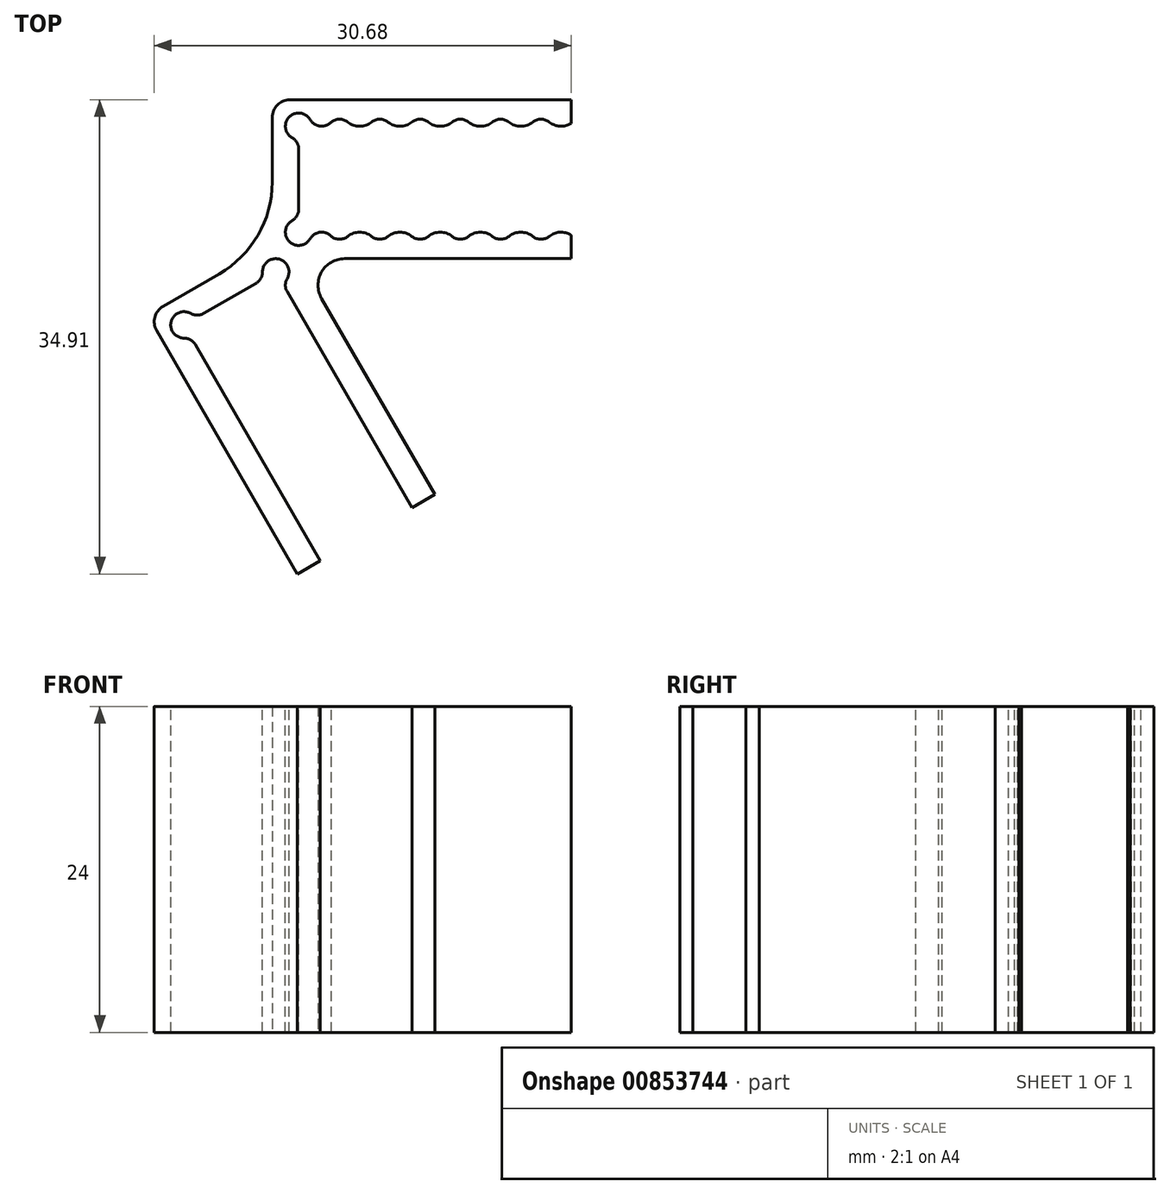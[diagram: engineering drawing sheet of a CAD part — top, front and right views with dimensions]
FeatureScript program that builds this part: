
annotation { "Feature Type Name" : "Feature", "Feature Type Description" : "" }
export const myFeature = defineFeature(function(context is Context, id is Id, definition is map)
    precondition{}
    {
        {
            var Q0;
            Q0=qCreatedBy(makeId("Top.planeOp"),FACE);
            var sketch = newSketch(context, id + "F0", { "sketchPlane" : qUnion([Q0])});
            skCircle(sketch, "E0.cCircle", {"center": v(0, 0) * mm, "radius": 33.77 * mm, "construction": true});
            skLineSegment(sketch, "E0.0", {"start": v(58.5, 33.77) * mm, "end": v(0, -67.55) * mm, "construction": true});
            skLineSegment(sketch, "E0.1", {"start": v(0, -67.55) * mm, "end": v(-58.5, 33.77) * mm, "construction": true});
            skLineSegment(sketch, "E0.2", {"start": v(-58.5, 33.77) * mm, "end": v(58.5, 33.77) * mm, "construction": true});
            skPoint(sketch, "E0.0.midPoint", {"position": v(29.25, -16.89) * mm});
            skSolve(sketch);
        }
        {
            var Q0;
            Q0=qCreatedBy(makeId("Top.planeOp"),FACE);
            var sketch = newSketch(context, id + "F1", { "sketchPlane" : qUnion([Q0])});
            skLineSegment(sketch, "E1", {"start": v(-58.5, 33.77) * mm, "end": v(0, 0) * mm, "construction": true});
            skLineSegment(sketch, "E2.0", {"start": v(-58.5, 35.72) * mm, "end": v(-38.45, 35.72) * mm});
            skLineSegment(sketch, "E3", {"start": v(-58.5, 35.72) * mm, "end": v(-58.5, 43.52) * mm});
            skLineSegment(sketch, "E4", {"start": v(-58.5, 43.52) * mm, "end": v(-38.45, 43.52) * mm});
            skLineSegment(sketch, "E5.0", {"start": v(-60.45, 45.47) * mm, "end": v(-38.45, 45.47) * mm});
            skLineSegment(sketch, "E5.1", {"start": v(-60.45, 34.9) * mm, "end": v(-60.45, 45.47) * mm});
            skLineSegment(sketch, "E5.2", {"start": v(-58.5, 33.77) * mm, "end": v(-38.45, 33.77) * mm});
            skLineSegment(sketch, "E6", {"start": v(-38.45, 45.47) * mm, "end": v(-38.45, 43.52) * mm});
            skLineSegment(sketch, "E7.trimOffspring", {"start": v(-38.45, 35.72) * mm, "end": v(-38.45, 33.77) * mm});
            skLineSegment(sketch, "E8.MirrorCS", {"start": v(-50.16, 15.44) * mm, "end": v(-48.48, 16.41) * mm});
            skLineSegment(sketch, "E9.MirrorCS", {"start": v(-69.6, 29.61) * mm, "end": v(-58.6, 10.56) * mm});
            skLineSegment(sketch, "E10.MirrorCS", {"start": v(-66.94, 28.9) * mm, "end": v(-56.92, 11.54) * mm});
            skLineSegment(sketch, "E11.MirrorCS", {"start": v(-60.19, 32.8) * mm, "end": v(-66.94, 28.9) * mm});
            skLineSegment(sketch, "E12.MirrorCS", {"start": v(-60.45, 34.9) * mm, "end": v(-69.6, 29.61) * mm});
            skLineSegment(sketch, "E13.MirrorCS", {"start": v(-58.6, 10.56) * mm, "end": v(-56.92, 11.54) * mm});
            skLineSegment(sketch, "E14", {"start": v(-58.5, 33.77) * mm, "end": v(-48.48, 16.41) * mm});
            skLineSegment(sketch, "E15", {"start": v(-50.16, 15.44) * mm, "end": v(-60.19, 32.8) * mm});
            skSolve(sketch);
        }
        {
            var Q0;
            Q0 = qSketchRegion(id + "F1", true);
            extrude(context, id + "F2", {"entities" : qUnion([Q0]), "depth" : 24 * mm, "offsetDistance" : 25 * mm});
        }
        {
            var Q0;
            Q0=makeQuery(id+"F2.opExtrude","SWEPT_EDGE",EDGE,{"disambiguationData":[OSD([sQuery(id+"F1.wireOp",EDGE,"E5.2"),sQuery(id+"F1.wireOp",EDGE,"E14")])]});
            fillet(context, id + "F3", {"entities" : qUnion([Q0]), "radius" : (7.8 / 4) * mm, "tangentPropagation" : true, "allowEdgeOverflow" : false});
        }
        {
            var Q0;
            Q0=makeQuery(id+"F2.opExtrude","SWEPT_EDGE",EDGE,{"disambiguationData":[OSD([sQuery(id+"F1.wireOp",EDGE,"E5.0"),sQuery(id+"F1.wireOp",EDGE,"E5.1")])]});
            var Q1;
            Q1=makeQuery(id+"F2.opExtrude","SWEPT_EDGE",EDGE,{"disambiguationData":[OSD([sQuery(id+"F1.wireOp",EDGE,"E9.MirrorCS"),sQuery(id+"F1.wireOp",EDGE,"E12.MirrorCS")])]});
            fillet(context, id + "F4", {"entities" : qUnion([Q0, Q1]), "radius" : (7.8 / 6) * mm, "tangentPropagation" : true, "allowEdgeOverflow" : false});
        }
        {
            var Q0;
            Q0=makeQuery(id+"F2.opExtrude","SWEPT_EDGE",EDGE,{"disambiguationData":[OSD([sQuery(id+"F1.wireOp",EDGE,"E5.1"),sQuery(id+"F1.wireOp",EDGE,"E12.MirrorCS")])]});
            fillet(context, id + "F5", {"entities" : qUnion([Q0]), "radius" : 7.8 * mm, "tangentPropagation" : true, "allowEdgeOverflow" : false});
        }
        {
            var Q0;
            Q0=makeQuery(id+"F2.opExtrude","CAP_FACE",FACE,{"disambiguationData":[OSD([sQuery(id+"F1.wireOp",EDGE,"E2.0"),sQuery(id+"F1.wireOp",EDGE,"E3"),sQuery(id+"F1.wireOp",EDGE,"E4"),sQuery(id+"F1.wireOp",EDGE,"E5.0"),sQuery(id+"F1.wireOp",EDGE,"E5.1"),sQuery(id+"F1.wireOp",EDGE,"E5.2"),sQuery(id+"F1.wireOp",EDGE,"E6"),sQuery(id+"F1.wireOp",EDGE,"E7.trimOffspring"),sQuery(id+"F1.wireOp",EDGE,"E8.MirrorCS"),sQuery(id+"F1.wireOp",EDGE,"E9.MirrorCS"),sQuery(id+"F1.wireOp",EDGE,"E10.MirrorCS"),sQuery(id+"F1.wireOp",EDGE,"E11.MirrorCS"),sQuery(id+"F1.wireOp",EDGE,"E12.MirrorCS"),sQuery(id+"F1.wireOp",EDGE,"E13.MirrorCS"),sQuery(id+"F1.wireOp",EDGE,"E14"),sQuery(id+"F1.wireOp",EDGE,"E15")])],"isStart":false});
            var sketch = newSketch(context, id + "F6", { "sketchPlane" : qUnion([Q0])});
            skCircle(sketch, "E16", {"center": v(-58.5, 43.52) * mm, "radius": 0.97 * mm});
            skCircle(sketch, "E17", {"center": v(-58.5, 35.72) * mm, "radius": 0.97 * mm});
            skCircle(sketch, "E18", {"center": v(-60.19, 32.8) * mm, "radius": 0.97 * mm});
            skCircle(sketch, "E19", {"center": v(-66.94, 28.9) * mm, "radius": 0.97 * mm});
            skSolve(sketch);
        }
        {
            var Q0;
            Q0 = qSketchRegion(id + "F6", true);
            extrude(context, id + "F7", {"entities" : qUnion([Q0]), "operationType" : NewBodyOperationType.REMOVE, "endBound" : BoundingType.THROUGH_ALL, "oppositeDirection" : true, "depth" : 25 * mm, "offsetDistance" : 25 * mm});
        }
        {
            var Q0;
            Q0=makeQuery(id+"F7.boolean.opBoolean","INTERSECT",EDGE,{"derivedFrom":[makeQuery(id+"F2.opExtrude","SWEPT_FACE",FACE,{"disambiguationData":[OSD([sQuery(id+"F1.wireOp",EDGE,"E4")])]}),makeQuery(id+"F7.opExtrude","SWEPT_FACE",FACE,{"disambiguationData":[OSD([sQuery(id+"F6.wireOp",EDGE,"E16")])]})]});
            var Q1;
            Q1=makeQuery(id+"F7.boolean.opBoolean","INTERSECT",EDGE,{"derivedFrom":[makeQuery(id+"F2.opExtrude","SWEPT_FACE",FACE,{"disambiguationData":[OSD([sQuery(id+"F1.wireOp",EDGE,"E3")])]}),makeQuery(id+"F7.opExtrude","SWEPT_FACE",FACE,{"disambiguationData":[OSD([sQuery(id+"F6.wireOp",EDGE,"E16")])]})]});
            var Q2;
            Q2=makeQuery(id+"F7.boolean.opBoolean","INTERSECT",EDGE,{"derivedFrom":[makeQuery(id+"F2.opExtrude","SWEPT_FACE",FACE,{"disambiguationData":[OSD([sQuery(id+"F1.wireOp",EDGE,"E3")])]}),makeQuery(id+"F7.opExtrude","SWEPT_FACE",FACE,{"disambiguationData":[OSD([sQuery(id+"F6.wireOp",EDGE,"E17")])]})]});
            var Q3;
            Q3=makeQuery(id+"F7.boolean.opBoolean","INTERSECT",EDGE,{"derivedFrom":[makeQuery(id+"F2.opExtrude","SWEPT_FACE",FACE,{"disambiguationData":[OSD([sQuery(id+"F1.wireOp",EDGE,"E11.MirrorCS")])]}),makeQuery(id+"F7.opExtrude","SWEPT_FACE",FACE,{"disambiguationData":[OSD([sQuery(id+"F6.wireOp",EDGE,"E18")])]})]});
            var Q4;
            Q4=makeQuery(id+"F7.boolean.opBoolean","INTERSECT",EDGE,{"derivedFrom":[makeQuery(id+"F2.opExtrude","SWEPT_FACE",FACE,{"disambiguationData":[OSD([sQuery(id+"F1.wireOp",EDGE,"E11.MirrorCS")])]}),makeQuery(id+"F7.opExtrude","SWEPT_FACE",FACE,{"disambiguationData":[OSD([sQuery(id+"F6.wireOp",EDGE,"E19")])]})]});
            var Q5;
            Q5=makeQuery(id+"F7.boolean.opBoolean","INTERSECT",EDGE,{"derivedFrom":[makeQuery(id+"F2.opExtrude","SWEPT_FACE",FACE,{"disambiguationData":[OSD([sQuery(id+"F1.wireOp",EDGE,"E10.MirrorCS")])]}),makeQuery(id+"F7.opExtrude","SWEPT_FACE",FACE,{"disambiguationData":[OSD([sQuery(id+"F6.wireOp",EDGE,"E19")])]})]});
            var Q6;
            Q6=makeQuery(id+"F7.boolean.opBoolean","INTERSECT",EDGE,{"derivedFrom":[makeQuery(id+"F2.opExtrude","SWEPT_FACE",FACE,{"disambiguationData":[OSD([sQuery(id+"F1.wireOp",EDGE,"E15")])]}),makeQuery(id+"F7.opExtrude","SWEPT_FACE",FACE,{"disambiguationData":[OSD([sQuery(id+"F6.wireOp",EDGE,"E18")])]})]});
            var Q7;
            Q7=makeQuery(id+"F7.boolean.opBoolean","INTERSECT",EDGE,{"derivedFrom":[makeQuery(id+"F2.opExtrude","SWEPT_FACE",FACE,{"disambiguationData":[OSD([sQuery(id+"F1.wireOp",EDGE,"E2.0")])]}),makeQuery(id+"F7.opExtrude","SWEPT_FACE",FACE,{"disambiguationData":[OSD([sQuery(id+"F6.wireOp",EDGE,"E17")])]})]});
            fillet(context, id + "F8", {"entities" : qUnion([Q0, Q1, Q2, Q3, Q4, Q5, Q6, Q7]), "radius" : (7.8 / 8) * mm, "tangentPropagation" : true, "allowEdgeOverflow" : false});
        }
        {
            var Q0;
            Q0=makeQuery(id+"F2.opExtrude","CAP_FACE",FACE,{"disambiguationData":[OSD([sQuery(id+"F1.wireOp",EDGE,"E2.0"),sQuery(id+"F1.wireOp",EDGE,"E3"),sQuery(id+"F1.wireOp",EDGE,"E4"),sQuery(id+"F1.wireOp",EDGE,"E5.0"),sQuery(id+"F1.wireOp",EDGE,"E5.1"),sQuery(id+"F1.wireOp",EDGE,"E5.2"),sQuery(id+"F1.wireOp",EDGE,"E6"),sQuery(id+"F1.wireOp",EDGE,"E7.trimOffspring"),sQuery(id+"F1.wireOp",EDGE,"E8.MirrorCS"),sQuery(id+"F1.wireOp",EDGE,"E9.MirrorCS"),sQuery(id+"F1.wireOp",EDGE,"E10.MirrorCS"),sQuery(id+"F1.wireOp",EDGE,"E11.MirrorCS"),sQuery(id+"F1.wireOp",EDGE,"E12.MirrorCS"),sQuery(id+"F1.wireOp",EDGE,"E13.MirrorCS"),sQuery(id+"F1.wireOp",EDGE,"E14"),sQuery(id+"F1.wireOp",EDGE,"E15")])],"isStart":false});
            var sketch = newSketch(context, id + "F9", { "sketchPlane" : qUnion([Q0])});
            skArc(sketch, "E20", {"start": v(-56.1, 35.42) * mm, "mid": v(-56.42, 35.65) * mm, "end": v(-56.81, 35.72) * mm});
            skArc(sketch, "E21", {"start": v(-56.1, 35.42) * mm, "mid": v(-55.5, 35.2) * mm, "end": v(-54.88, 35.42) * mm});
            skLineSegment(sketch, "E22", {"start": v(-56.77, 35.42) * mm, "end": v(-38.45, 35.42) * mm, "construction": true});
            skArc(sketch, "E23", {"start": v(-54.88, 35.42) * mm, "mid": v(-54.01, 35.72) * mm, "end": v(-53.14, 35.42) * mm});
            skArc(sketch, "E24.1.0.0", {"start": v(-53.14, 35.42) * mm, "mid": v(-52.53, 35.2) * mm, "end": v(-51.92, 35.42) * mm});
            skArc(sketch, "E24.1.0.1", {"start": v(-51.92, 35.42) * mm, "mid": v(-51.04, 35.72) * mm, "end": v(-50.17, 35.42) * mm});
            skArc(sketch, "E24.2.0.0", {"start": v(-50.17, 35.42) * mm, "mid": v(-49.56, 35.2) * mm, "end": v(-48.95, 35.42) * mm});
            skArc(sketch, "E24.2.0.1", {"start": v(-48.95, 35.42) * mm, "mid": v(-48.08, 35.72) * mm, "end": v(-47.2, 35.42) * mm});
            skArc(sketch, "E24.3.0.0", {"start": v(-47.2, 35.42) * mm, "mid": v(-46.6, 35.2) * mm, "end": v(-45.99, 35.42) * mm});
            skArc(sketch, "E24.3.0.1", {"start": v(-45.99, 35.42) * mm, "mid": v(-45.11, 35.72) * mm, "end": v(-44.24, 35.42) * mm});
            skArc(sketch, "E24.4.0.0", {"start": v(-44.24, 35.42) * mm, "mid": v(-43.63, 35.2) * mm, "end": v(-43.02, 35.42) * mm});
            skArc(sketch, "E24.4.0.1", {"start": v(-43.02, 35.42) * mm, "mid": v(-42.15, 35.72) * mm, "end": v(-41.28, 35.42) * mm});
            skArc(sketch, "E24.5.0.0", {"start": v(-41.28, 35.42) * mm, "mid": v(-40.67, 35.2) * mm, "end": v(-40.06, 35.42) * mm});
            skArc(sketch, "E24.5.0.1", {"start": v(-40.06, 35.42) * mm, "mid": v(-39.18, 35.72) * mm, "end": v(-38.31, 35.42) * mm});
            skLineSegment(sketch, "E25", {"start": v(-38.45, 35.72) * mm, "end": v(-38.45, 43.52) * mm, "construction": true});
            skLineSegment(sketch, "E26", {"start": v(-38.45, 39.62) * mm, "end": v(-58.5, 39.62) * mm, "construction": true});
            skLineSegment(sketch, "E27", {"start": v(-56.81, 35.72) * mm, "end": v(-56.81, 43.52) * mm});
            skArc(sketch, "E28.MirrorCS", {"start": v(-56.1, 43.83) * mm, "mid": v(-56.42, 43.6) * mm, "end": v(-56.81, 43.52) * mm});
            skArc(sketch, "E29.MirrorCS", {"start": v(-56.1, 43.83) * mm, "mid": v(-55.5, 44.04) * mm, "end": v(-54.88, 43.83) * mm});
            skArc(sketch, "E30.MirrorCS", {"start": v(-54.88, 43.83) * mm, "mid": v(-54.01, 43.52) * mm, "end": v(-53.14, 43.83) * mm});
            skArc(sketch, "E31.MirrorCS", {"start": v(-51.92, 43.83) * mm, "mid": v(-51.04, 43.52) * mm, "end": v(-50.17, 43.83) * mm});
            skArc(sketch, "E32.MirrorCS", {"start": v(-53.14, 43.83) * mm, "mid": v(-52.53, 44.04) * mm, "end": v(-51.92, 43.83) * mm});
            skArc(sketch, "E33.MirrorCS", {"start": v(-50.17, 43.83) * mm, "mid": v(-49.56, 44.04) * mm, "end": v(-48.95, 43.83) * mm});
            skArc(sketch, "E34.MirrorCS", {"start": v(-48.95, 43.83) * mm, "mid": v(-48.08, 43.52) * mm, "end": v(-47.2, 43.83) * mm});
            skArc(sketch, "E35.MirrorCS", {"start": v(-47.2, 43.83) * mm, "mid": v(-46.6, 44.04) * mm, "end": v(-45.99, 43.83) * mm});
            skArc(sketch, "E36.MirrorCS", {"start": v(-45.99, 43.83) * mm, "mid": v(-45.11, 43.52) * mm, "end": v(-44.24, 43.83) * mm});
            skArc(sketch, "E37.MirrorCS", {"start": v(-44.24, 43.83) * mm, "mid": v(-43.63, 44.04) * mm, "end": v(-43.02, 43.83) * mm});
            skArc(sketch, "E38.MirrorCS", {"start": v(-43.02, 43.83) * mm, "mid": v(-42.15, 43.52) * mm, "end": v(-41.28, 43.83) * mm});
            skArc(sketch, "E39.MirrorCS", {"start": v(-41.28, 43.83) * mm, "mid": v(-40.67, 44.04) * mm, "end": v(-40.06, 43.83) * mm});
            skArc(sketch, "E40.MirrorCS", {"start": v(-40.06, 43.83) * mm, "mid": v(-39.18, 43.52) * mm, "end": v(-38.31, 43.83) * mm});
            skLineSegment(sketch, "E41", {"start": v(-38.31, 43.83) * mm, "end": v(-38.31, 35.42) * mm});
            skSolve(sketch);
        }
        {
            var Q0;
            Q0 = qSketchRegion(id + "F9", true);
            extrude(context, id + "F10", {"entities" : qUnion([Q0]), "operationType" : NewBodyOperationType.REMOVE, "endBound" : BoundingType.THROUGH_ALL, "oppositeDirection" : true, "depth" : 25 * mm, "offsetDistance" : 25 * mm});
        }
        {
            var Q0;
            Q0=sQuery(id+"F1.wireOp",EDGE,"E1");
            cPlane(context, id + "F11", {"entities" : qUnion([Q0]), "cplaneType" : CPlaneType.LINE_ANGLE, "offset" : 25 * mm, "angle" : 0 * degree, "width" : 150 * mm, "height" : 150 * mm});
        }
    });
